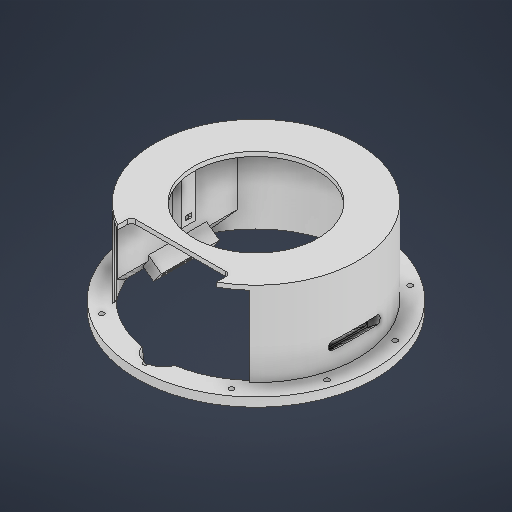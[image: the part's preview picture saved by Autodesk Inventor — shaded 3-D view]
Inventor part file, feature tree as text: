
AUTODESK INVENTOR PART (.ipt)
format: ipt  version: 2025 (Build 290162000, 162)  size: 520,704 bytes
history: native  units: in
note: dims shown in document units (in); Inventor stores cm internally (conversion verified against a paired STEP export)
features: extrude x17, sketch x15, plane x3, fillet x1, chamfer x1
ambient origin geometry x8: Origin, YZ Plane, XZ Plane, XY Plane, X Axis, Y Axis, Z Axis, Center Point
bodies: Solid1 (feature_tree)
feature tree (37):
  sketch  "Sketch1"  dims[d5=0.0in d7=0.0in]
  extrude  "Extrusion1"  TaperAngle=0.0deg  [1 undecoded]
  extrude  "Extrusion2"  Depth=4.5276in
  extrude  "Extrusion7"  Depth=0.2165in
  extrude  "Extrusion34"  Depth=6.1024in
  sketch  "Sketch30"  dims[d272=3.937in d273=4.1535in d274=0.0in d285=3.937in]
  plane  "Work Plane19"
  plane  "Work Plane21"
  plane  "Work Plane22"
  extrude  "Extrusion36"  Depth=4.1535in TaperAngle=0.0deg
  fillet  "Fillet19"  Radius=3.937in
  extrude  "Extrusion37"  Depth=2.0812in TaperAngle=0.0deg
  extrude  "Extrusion38"  Depth=0.1969in
  sketch  "Sketch35"  dims[d293=0.1969in d294=0.1969in]
  extrude  "Extrusion40"  Depth=1.5748in
  extrude  "Extrusion41"  Depth=0.1969in
  extrude  "Extrusion42"  Depth=0.3937in TaperAngle=0.0deg
  extrude  "Extrusion43"  Depth=1.7717in TaperAngle=0.0deg
  chamfer  "Chamfer14"  Distance=0.5906in
  sketch  "Sketch38"  dims[d301=2.9528in]
  extrude  "Extrusion44"  Depth=0.0689in
  extrude  "Extrusion45"  Depth=0.0689in TaperAngle=0.0deg
  sketch  "Sketch39"  dims[d308=6.378in]
  extrude  "Extrusion46"  Depth=0.0689in TaperAngle=0.0deg
  extrude  "Extrusion47"  Depth=0.0689in TaperAngle=0.0deg
  sketch  "Sketch43"  dims[d312=6.8898in d313=5.5413in d314=0.2362in d315=0.1969in d316=0.0in d317=0.1969in d318=0.0in d319=1.378in d320=0.0in d321=0.5906in d322=0.7874in d323=45.0deg d324=1.0in d326=0.315in d328=0.0in d329=0.0in d330=0.1772in d331=0.315in d332=0.0in d333=1.0in d334=0.2953in d335=0.1772in d336=0.0in d337=0.0in d338=0.315in d339=0.0in d340=0.8661in d341=0.8661in d344=0.5906in d345=0.5906in d346=0.5906in d347=0.5906in d348=0.5906in d349=0.0in d350=0.1969in d351=0.0in d352=0.5906in d353=0.5906in d354=0.5906in d355=0.5906in d356=0.5906in d357=0.1969in d358=0.0in d359=0.0in d360=0.0in d361=0.0689in d113=0.0197in d114=0.0344in d115=0.0197in d116=0.0344in d167=0.0197in d168=0.0344in d169=0.0197in d170=0.0344in d215=0.0197in d216=0.0344in d217=0.0197in d218=0.0344in d219=0.0in d220=0.0in d254=0.0197in d255=0.0344in d256=0.0197in d257=0.0344in]
  extrude  "Extrusion49"  Depth=0.5906in TaperAngle=45.0deg
  extrude  "Extrusion50"  Depth=0.0689in
  sketch  "Sketch2"  dims[d18=0.0in d52=4.5276in]
  sketch  "Sketch Circular Pattern5"  dims[d264=9.8425in d265=0.2165in]
  sketch  "Sketch28"  dims[d266=3.937in d268=360.0deg d271=6.1024in]
  sketch  "Sketch31"  dims[d286=1.5748in d287=2.0812in d288=0.0in]
  sketch  "Sketch32"  dims[d289=3.5039in d290=0.1969in]
  sketch  "Sketch33"  dims[d291=4.4094in d292=1.5748in]
  sketch  "Sketch36"  dims[d295=3.3465in d296=0.3937in d297=0.0in]
  sketch  "Sketch37"  dims[d298=0.6299in d299=1.7717in d300=0.0in]
  sketch  "Sketch42"  dims[d309=0.2805in d310=0.5906in d311=0.0in]
note: 1 required parameter value undecoded (feature->parameter linkage not recoverable at this tier; creation-order binding heuristic only, values carry confidence <= 0.55)
